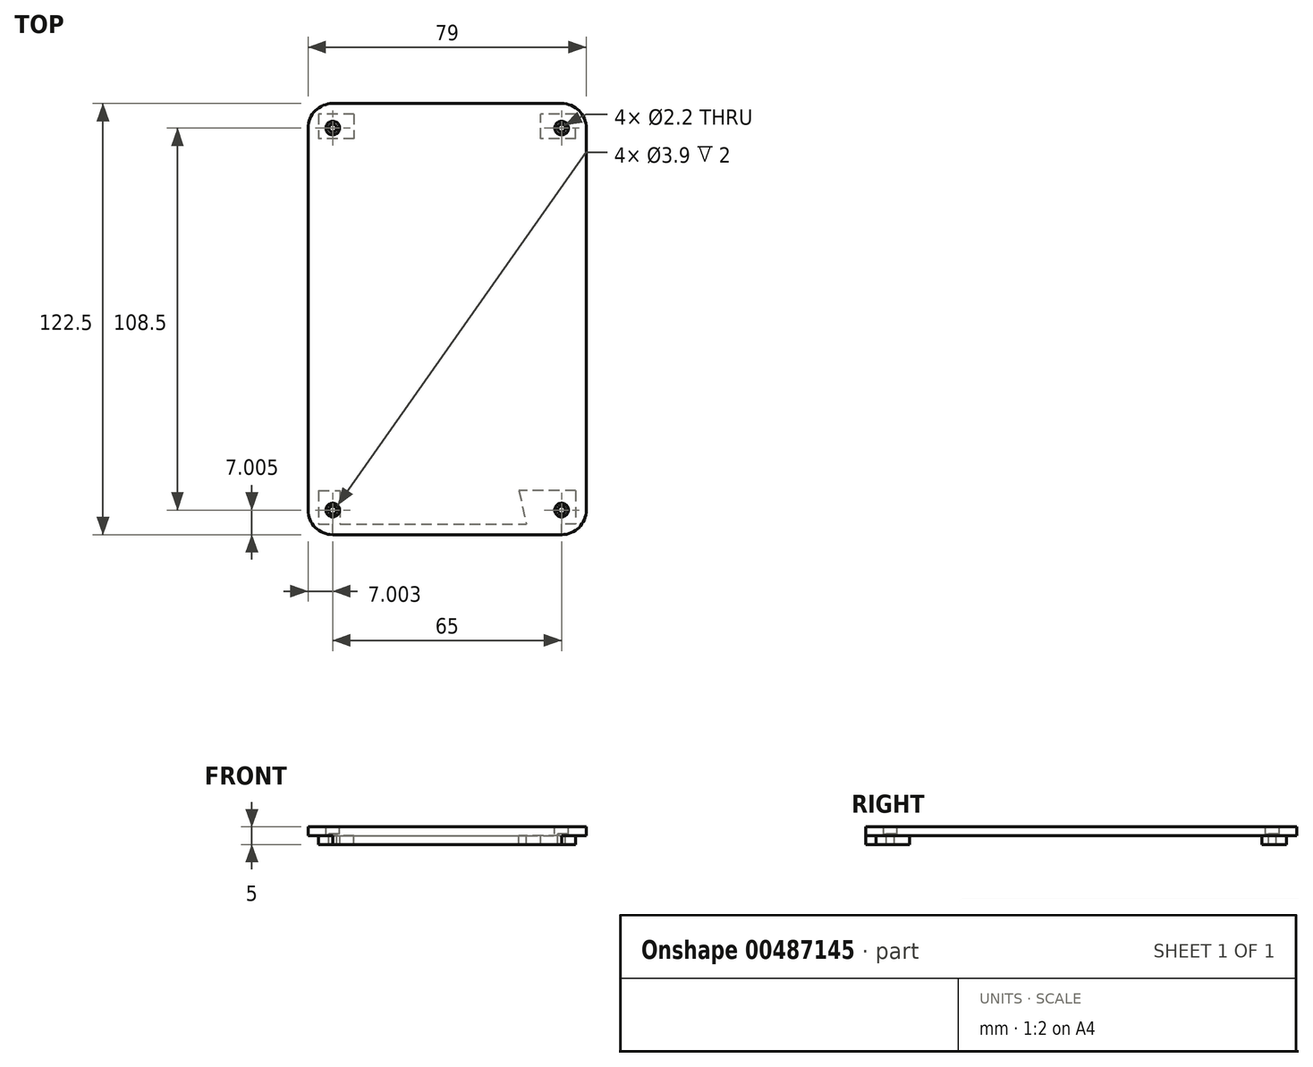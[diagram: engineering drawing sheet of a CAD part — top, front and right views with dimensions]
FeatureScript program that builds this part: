
annotation { "Feature Type Name" : "Feature", "Feature Type Description" : "" }
export const myFeature = defineFeature(function(context is Context, id is Id, definition is map)
    precondition{}
    {
        {
            var Q0;
            Q0=qCreatedBy(makeId("Top.planeOp"),FACE);
            var sketch = newSketch(context, id + "F0", { "sketchPlane" : qUnion([Q0])});
            skLineSegment(sketch, "E0.bottom", {"start": v(-32.56, 61.92) * mm, "end": v(32.44, 61.92) * mm});
            skLineSegment(sketch, "E0.top", {"start": v(-32.56, -60.58) * mm, "end": v(32.44, -60.58) * mm});
            skLineSegment(sketch, "E0.left", {"start": v(-39.56, 54.92) * mm, "end": v(-39.56, -53.58) * mm});
            skLineSegment(sketch, "E0.right", {"start": v(39.44, 54.92) * mm, "end": v(39.44, -53.58) * mm});
            skPoint(sketch, "E1.visualSharp", {"position": v(-39.56, 61.92) * mm});
            skArc(sketch, "E1.filletArc", {"start": v(-32.56, 61.92) * mm, "mid": v(-37.5, 59.87) * mm, "end": v(-39.56, 54.92) * mm});
            skPoint(sketch, "E2.visualSharp", {"position": v(39.44, 61.92) * mm});
            skArc(sketch, "E2.filletArc", {"start": v(39.44, 54.92) * mm, "mid": v(37.4, 59.87) * mm, "end": v(32.44, 61.92) * mm});
            skPoint(sketch, "E3.visualSharp", {"position": v(-39.56, -60.58) * mm});
            skArc(sketch, "E3.filletArc", {"start": v(-39.56, -53.58) * mm, "mid": v(-37.5, -58.53) * mm, "end": v(-32.56, -60.58) * mm});
            skPoint(sketch, "E4.visualSharp", {"position": v(39.44, -60.58) * mm});
            skArc(sketch, "E4.filletArc", {"start": v(32.44, -60.58) * mm, "mid": v(37.4, -58.53) * mm, "end": v(39.44, -53.58) * mm});
            skLineSegment(sketch, "E5.bottom", {"start": v(-32.56, 58.92) * mm, "end": v(32.44, 58.92) * mm});
            skLineSegment(sketch, "E5.top", {"start": v(-32.56, -57.58) * mm, "end": v(32.44, -57.58) * mm});
            skLineSegment(sketch, "E5.left", {"start": v(-36.56, 54.92) * mm, "end": v(-36.56, -53.58) * mm});
            skLineSegment(sketch, "E5.right", {"start": v(36.44, 54.92) * mm, "end": v(36.44, -53.58) * mm});
            skPoint(sketch, "E6.visualSharp", {"position": v(-36.56, 58.92) * mm});
            skArc(sketch, "E6.filletArc", {"start": v(-32.56, 58.92) * mm, "mid": v(-35.39, 57.75) * mm, "end": v(-36.56, 54.92) * mm});
            skPoint(sketch, "E7.visualSharp", {"position": v(36.44, 58.92) * mm});
            skArc(sketch, "E7.filletArc", {"start": v(36.44, 54.92) * mm, "mid": v(35.27, 57.75) * mm, "end": v(32.44, 58.92) * mm});
            skPoint(sketch, "E8.visualSharp", {"position": v(-36.56, -57.58) * mm});
            skArc(sketch, "E8.filletArc", {"start": v(-36.56, -53.58) * mm, "mid": v(-35.39, -56.4) * mm, "end": v(-32.56, -57.58) * mm});
            skPoint(sketch, "E9.visualSharp", {"position": v(36.44, -57.58) * mm});
            skArc(sketch, "E9.filletArc", {"start": v(32.44, -57.58) * mm, "mid": v(35.27, -56.4) * mm, "end": v(36.44, -53.58) * mm});
            skSolve(sketch);
        }
        {
            var Q0;
            Q0=qCreatedBy(makeId("Top.planeOp"),FACE);
            var sketch = newSketch(context, id + "F1", { "sketchPlane" : qUnion([Q0])});
            skLineSegment(sketch, "E10.bottom", {"start": v(-34.66, 51.92) * mm, "end": v(34.54, 51.92) * mm});
            skLineSegment(sketch, "E10.top", {"start": v(-34.66, -48.08) * mm, "end": v(34.54, -48.08) * mm});
            skLineSegment(sketch, "E10.left", {"start": v(-34.66, 51.92) * mm, "end": v(-34.66, -48.08) * mm});
            skLineSegment(sketch, "E10.right", {"start": v(34.54, 51.92) * mm, "end": v(34.54, -48.08) * mm});
            skSolve(sketch);
        }
        {
            var Q0;
            Q0=qCreatedBy(makeId("Top.planeOp"),FACE);
            cPlane(context, id + "F2", {"entities" : qUnion([Q0]), "cplaneType" : CPlaneType.OFFSET, "offset" : 2.5 * mm, "width" : 150 * mm, "height" : 150 * mm});
        }
        {
            var Q0;
            Q0=qCreatedBy(id+"F2.planeOp",FACE);
            var sketch = newSketch(context, id + "F3", { "sketchPlane" : qUnion([Q0])});
            skLineSegment(sketch, "E11.bottom", {"start": v(-34.66, 9.42) * mm, "end": v(-36.56, 9.42) * mm});
            skLineSegment(sketch, "E11.top", {"start": v(-34.66, -5.58) * mm, "end": v(-36.56, -5.58) * mm});
            skLineSegment(sketch, "E11.left", {"start": v(-34.66, 9.42) * mm, "end": v(-34.66, -5.58) * mm});
            skLineSegment(sketch, "E11.right", {"start": v(-36.56, 9.42) * mm, "end": v(-36.56, -5.58) * mm});
            skLineSegment(sketch, "E12.bottom", {"start": v(36.44, 9.42) * mm, "end": v(34.54, 9.42) * mm});
            skLineSegment(sketch, "E12.top", {"start": v(36.44, -5.58) * mm, "end": v(34.54, -5.58) * mm});
            skLineSegment(sketch, "E12.left", {"start": v(36.44, 9.42) * mm, "end": v(36.44, -5.58) * mm});
            skLineSegment(sketch, "E12.right", {"start": v(34.54, 9.42) * mm, "end": v(34.54, -5.58) * mm});
            skLineSegment(sketch, "E13.bottom", {"start": v(-36.56, -48.08) * mm, "end": v(-30.46, -48.08) * mm});
            skLineSegment(sketch, "E13.top", {"start": v(-36.56, -57.58) * mm, "end": v(-30.46, -57.58) * mm});
            skLineSegment(sketch, "E13.left", {"start": v(-36.56, -48.08) * mm, "end": v(-36.56, -57.58) * mm});
            skLineSegment(sketch, "E13.right", {"start": v(-30.46, -48.08) * mm, "end": v(-30.46, -57.58) * mm});
            skLineSegment(sketch, "E14.bottom", {"start": v(36.44, -48.08) * mm, "end": v(20.34, -48.08) * mm});
            skLineSegment(sketch, "E14.top", {"start": v(36.44, -57.58) * mm, "end": v(22.44, -57.58) * mm});
            skLineSegment(sketch, "E14.left", {"start": v(36.44, -48.08) * mm, "end": v(36.44, -57.58) * mm});
            skLineSegment(sketch, "E14.right", {"start": v(20.34, -48.08) * mm, "end": v(20.34, -48.08) * mm});
            skLineSegment(sketch, "E15", {"start": v(20.34, -48.08) * mm, "end": v(22.44, -57.58) * mm});
            skLineSegment(sketch, "E16.bottom", {"start": v(-26.56, 58.92) * mm, "end": v(-36.56, 58.92) * mm});
            skLineSegment(sketch, "E16.top", {"start": v(-26.56, 51.92) * mm, "end": v(-36.56, 51.92) * mm});
            skLineSegment(sketch, "E16.left", {"start": v(-26.56, 58.92) * mm, "end": v(-26.56, 51.92) * mm});
            skLineSegment(sketch, "E16.right", {"start": v(-36.56, 58.92) * mm, "end": v(-36.56, 51.92) * mm});
            skLineSegment(sketch, "E17.bottom", {"start": v(36.44, 51.92) * mm, "end": v(26.44, 51.92) * mm});
            skLineSegment(sketch, "E17.top", {"start": v(36.44, 58.92) * mm, "end": v(26.44, 58.92) * mm});
            skLineSegment(sketch, "E17.left", {"start": v(36.44, 51.92) * mm, "end": v(36.44, 58.92) * mm});
            skLineSegment(sketch, "E17.right", {"start": v(26.44, 51.92) * mm, "end": v(26.44, 58.92) * mm});
            skSolve(sketch);
        }
        {
            var Q0;
            Q0=qCreatedBy(id+"F2.planeOp",FACE);
            var sketch = newSketch(context, id + "F4", { "sketchPlane" : qUnion([Q0])});
            skPoint(sketch, "E18", {"position": v(-32.56, 54.92) * mm});
            skPoint(sketch, "E19", {"position": v(32.44, 54.92) * mm});
            skPoint(sketch, "E20", {"position": v(32.44, -53.58) * mm});
            skPoint(sketch, "E21", {"position": v(-32.56, -53.58) * mm});
            skSolve(sketch);
        }
        {
            var Q0;
            Q0=makeQuery(id+"F0.imprint","IMPRINT",FACE,{"disambiguationData":[TD([[makeQuery(id+"F0.imprint","IMPRINT",EDGE,{"derivedFrom":sQuery(id+"F0.wireOp",EDGE,"E5.bottom")}),-1.0]])]});
            var Q1;
            Q1=makeQuery(id+"F0.imprint","IMPRINT",FACE,{"disambiguationData":[TD([[makeQuery(id+"F0.imprint","IMPRINT",EDGE,{"derivedFrom":sQuery(id+"F0.wireOp",EDGE,"E0.bottom")}),-1.0]])]});
            extrude(context, id + "F5", {"entities" : qUnion([Q0, Q1]), "depth" : 2.5 * mm});
        }
        {
            var Q0;
            Q0=qCreatedBy(id+"F2.planeOp",FACE);
            var sketch = newSketch(context, id + "F6", { "sketchPlane" : qUnion([Q0])});
            skLineSegment(sketch, "E22.bottom", {"start": v(-32.56, -60.58) * mm, "end": v(32.44, -60.58) * mm});
            skLineSegment(sketch, "E22.top", {"start": v(-32.56, -57.58) * mm, "end": v(32.44, -57.58) * mm});
            skLineSegment(sketch, "E22.left", {"start": v(-32.56, -60.58) * mm, "end": v(-32.56, -57.58) * mm});
            skLineSegment(sketch, "E22.right", {"start": v(32.44, -60.58) * mm, "end": v(32.44, -57.58) * mm});
            skSolve(sketch);
        }
        {
            var Q0;
            Q0=makeQuery(id+"F3.imprint","IMPRINT",FACE,{"disambiguationData":[TD([[makeQuery(id+"F3.imprint","IMPRINT",EDGE,{"derivedFrom":sQuery(id+"F3.wireOp",EDGE,"E17.bottom")}),-1.0]])]});
            var Q1;
            Q1=makeQuery(id+"F3.imprint","IMPRINT",FACE,{"disambiguationData":[TD([[makeQuery(id+"F3.imprint","IMPRINT",EDGE,{"derivedFrom":sQuery(id+"F3.wireOp",EDGE,"E16.bottom")}),1.0]])]});
            var Q2;
            Q2=makeQuery(id+"F3.imprint","IMPRINT",FACE,{"disambiguationData":[TD([[makeQuery(id+"F3.imprint","IMPRINT",EDGE,{"derivedFrom":sQuery(id+"F3.wireOp",EDGE,"E13.bottom")}),-1.0]])]});
            var Q3;
            Q3=makeQuery(id+"F3.imprint","IMPRINT",FACE,{"disambiguationData":[TD([[makeQuery(id+"F3.imprint","IMPRINT",EDGE,{"derivedFrom":sQuery(id+"F3.wireOp",EDGE,"E14.bottom")}),1.0]])]});
            extrude(context, id + "F7", {"entities" : qUnion([Q0, Q1, Q2, Q3]), "operationType" : NewBodyOperationType.ADD, "oppositeDirection" : true, "depth" : 5 * mm});
        }
        {
            var Q0;
            Q0=sQuery(id+"F4.wireOp",VERTEX,"E18");
            var Q1;
            Q1=sQuery(id+"F4.wireOp",VERTEX,"E19");
            var Q2;
            Q2=sQuery(id+"F4.wireOp",VERTEX,"E20");
            var Q3;
            Q3=sQuery(id+"F4.wireOp",VERTEX,"E21");
            var Q4;
            Q4=makeQuery(id+"F5.opExtrude","SWEPT_BODY",BODY,{"disambiguationData":[OSD([sQuery(id+"F0.wireOp",EDGE,"E0.bottom"),sQuery(id+"F0.wireOp",EDGE,"E0.top"),sQuery(id+"F0.wireOp",EDGE,"E0.left"),sQuery(id+"F0.wireOp",EDGE,"E0.right"),sQuery(id+"F0.wireOp",EDGE,"E1.filletArc"),sQuery(id+"F0.wireOp",EDGE,"E2.filletArc"),sQuery(id+"F0.wireOp",EDGE,"E3.filletArc"),sQuery(id+"F0.wireOp",EDGE,"E4.filletArc")])]});
            hole(context, id + "F8", {"style" : HoleStyle.C_BORE, "endStyle" : HoleEndStyle.BLIND, "holeDiameter" : 2.2 * mm, "cBoreDiameter" : 3.9 * mm, "cBoreDepth" : 2 * mm, "holeDepth" : 10 * mm, "isTappedThrough" : true, "tappedDepth" : 12 * mm, "tapClearance" : 3, "startFromSketch" : true, "locations" : qUnion([Q0, Q1, Q2, Q3]), "scope" : qUnion([Q4])});
        }
        {
            var Q0;
            Q0 = qSketchRegion(id + "F6", true);
            var Q1;
            Q1 = qConstructionFilter(qBodyType(qCreatedBy(id + "F6" ,EDGE), BodyType.WIRE), ConstructionObject.NO);
            extrude(context, id + "F9", {"entities" : qUnion([Q0]), "operationType" : NewBodyOperationType.ADD, "surfaceEntities" : qUnion([Q1]), "oppositeDirection" : true, "depth" : 5 * mm});
        }
    });
